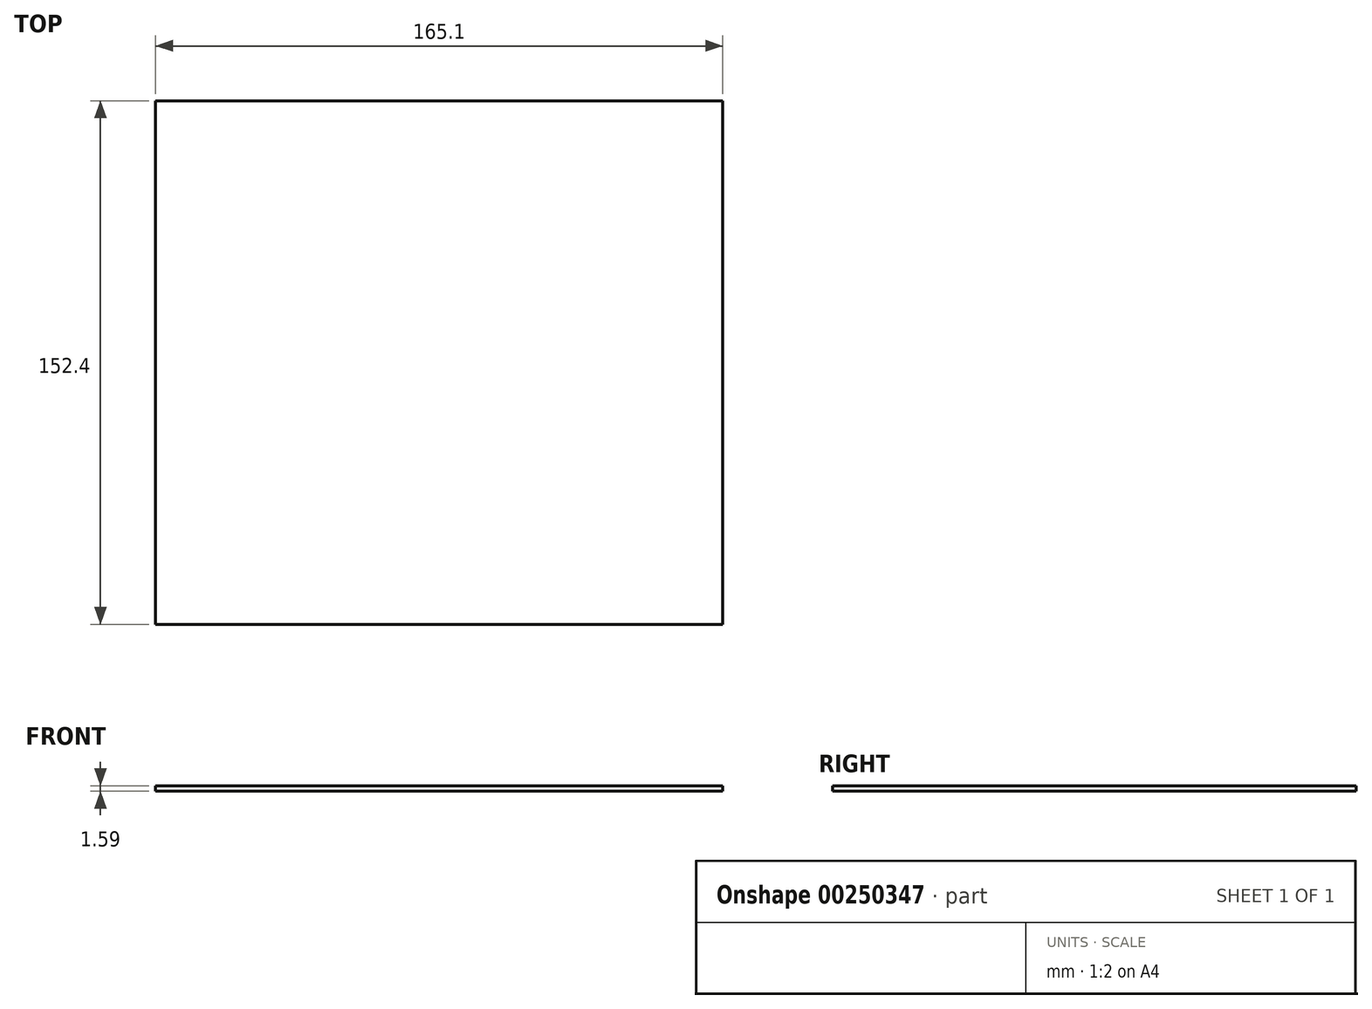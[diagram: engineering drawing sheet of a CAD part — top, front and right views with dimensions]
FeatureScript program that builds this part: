
annotation { "Feature Type Name" : "Feature", "Feature Type Description" : "" }
export const myFeature = defineFeature(function(context is Context, id is Id, definition is map)
    precondition{}
    {
        {
            var Q0;
            Q0=qCreatedBy(makeId("Top.planeOp"),FACE);
            var sketch = newSketch(context, id + "F0", { "sketchPlane" : qUnion([Q0])});
            skLineSegment(sketch, "E0.bottom", {"start": v(82.55, 76.2) * mm, "end": v(-82.55, 76.2) * mm});
            skLineSegment(sketch, "E0.top", {"start": v(82.55, -76.2) * mm, "end": v(-82.55, -76.2) * mm});
            skLineSegment(sketch, "E0.left", {"start": v(82.55, 76.2) * mm, "end": v(82.55, -76.2) * mm});
            skLineSegment(sketch, "E0.right", {"start": v(-82.55, 76.2) * mm, "end": v(-82.55, -76.2) * mm});
            skPoint(sketch, "E0.middle", {"position": v(0, 0) * mm});
            skSolve(sketch);
        }
        {
            var Q0;
            Q0 = qSketchRegion(id + "F0", true);
            extrude(context, id + "F1", {"entities" : qUnion([Q0]), "depth" : 1.59 * mm});
        }
    });
